# Revit family: 12147 Велопарковка VELO-15 Хоббика
name_source: partatom
category: Антураж
revit_build: Autodesk Revit 2018 (Build: 20180423_1000(x64)
units: mm (PartAtom-declared; Revit-internal decimal feet)

## family parameters
Всегда вертикально = Да
Источник визуального образа = Геометрия семейства
На основе рабочей плоскости = Нет
Общий = Нет
При загрузке вырезать с полостями = Нет
Точка расчета площади = Нет

## types (3) — shared parameters
URL = https://hobbyka.ru
Артикул товара = Арт. 12147
Высота = 960 мм
Группа модели = Велопарковки
Изготовитель = ООО «Хоббика»
Изображение типоразмера = Велопарковка VELO-15 Арт 12147.jpg
Цвет каркаса = Сталь
Ширина = 505 мм

## per-type parameters (varying)
| type | 10 мест | 10 мест ПВХ | 6 мест | Длина | Кол-во мест | Материал изделия | Описание |
| 6 мест | Нет | Нет | Да | 1755 мм | 6 | Сталь | Велопарковка VELO-15. Версия 6 мест |
| 10 мест | Да | Нет | Нет | 3010 мм | 10 | Сталь | Велопарковка VELO-15. Версия 10 мест |
| 10 мест ПВХ | Нет | Да | Нет | 3010 мм | 10 | Сталь, ПВХ | Велопарковка VELO-15. Версия 10 мест с ПВХ панелью |
